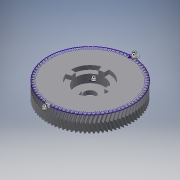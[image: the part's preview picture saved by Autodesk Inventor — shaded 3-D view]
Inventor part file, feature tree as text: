
AUTODESK INVENTOR PART (.ipt)
format: ipt  version: 2017 (Build 210142000, 142)  size: 1,868,288 bytes
history: native  units: mm
features: sketch x5, extrude x5, pattern_circular x3, helix x2, projected_geometry x1
ambient origin geometry x8: Origin, YZ Plane, XZ Plane, XY Plane, X Axis, Y Axis, Z Axis, Center Point
bodies: Solid1 (feature_tree)
feature tree (16):
  sketch  "Sketch1"  dims[d0=20.0mm d1=0.0mm]
  extrude  "Extrusion1"  TaperAngle=0.0deg  [1 undecoded]
  extrude  "Extrusion2"  Depth=810.0mm TaperAngle=360.0deg
  pattern_circular  "Circular Pattern1"  [2 undecoded]
  extrude  "Extrusion3"  Depth=6.0mm
  extrude  "Extrusion4"  Depth=12.217305mm
  extrude  "Extrusion5"  Depth=5.0mm TaperAngle=0.0deg
  pattern_circular  "Circular Pattern2"  Count=4 Angle=360.0deg
  helix  "Coil1"  [1 undecoded]
  helix  "Coil2"  [1 undecoded]
  pattern_circular  "Circular Pattern3"  [2 undecoded]
  sketch  "Sketch2"  dims[d2=10.0mm d3=0.0mm d4=810.0mm d5=360.0deg]
  sketch  "Sketch3"  dims[d7=13.5mm]
  sketch  "Sketch4"  dims[d8=10.0mm d9=0.0mm]
  sketch  "Sketch5"  dims[d10=35.0mm d11=15.0mm d12=0.0mm d13=6.0mm d14=12.217305mm d15=5.0mm d16=0.0mm d17=40.0mm d18=360.0deg d20=10.0mm d21=10.0mm d22=0.1mm d23=0.0mm d24=90.0deg d25=90.0deg d26=0.0mm d27=0.0mm d28=10.0mm d29=10.0mm d30=0.1mm d31=0.0mm d32=90.0deg d33=90.0deg d34=0.0mm d35=0.0mm d36=810.0mm d37=360.0deg]
  projected_geometry  "Projected Loop1"
note: 7 required parameter values undecoded (feature->parameter linkage not recoverable at this tier; creation-order binding heuristic only, values carry confidence <= 0.55)
